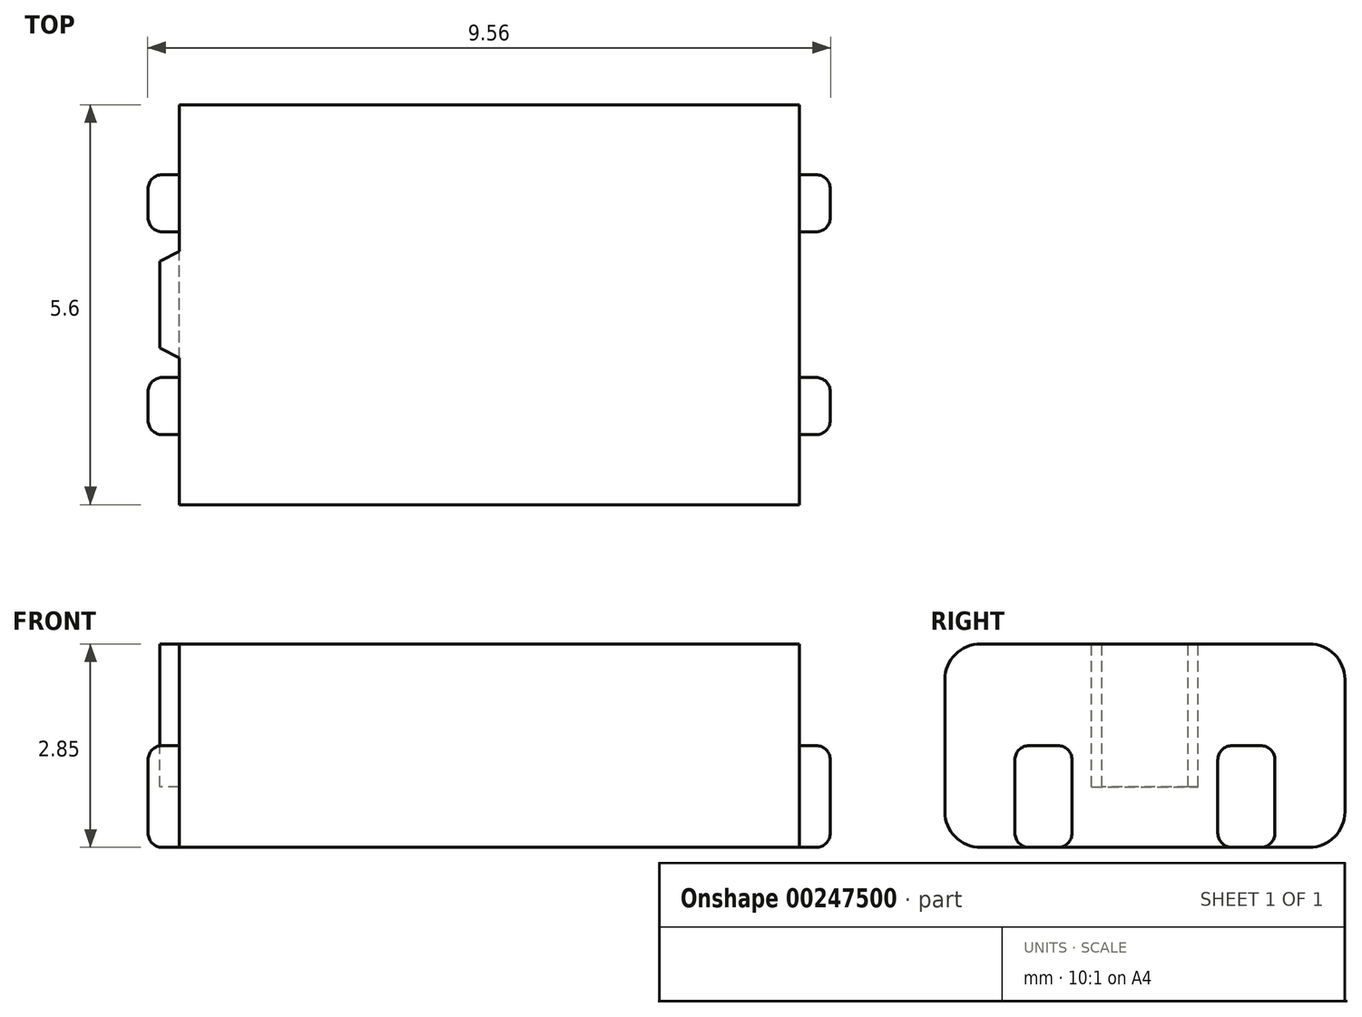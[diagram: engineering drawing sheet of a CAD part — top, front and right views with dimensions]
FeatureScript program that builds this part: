
annotation { "Feature Type Name" : "Feature", "Feature Type Description" : "" }
export const myFeature = defineFeature(function(context is Context, id is Id, definition is map)
    precondition{}
    {
        {
            var Q0;
            Q0=qCreatedBy(makeId("Top.planeOp"),FACE);
            var sketch = newSketch(context, id + "F0", { "sketchPlane" : qUnion([Q0])});
            skLineSegment(sketch, "E0.bottom", {"start": v(4.34, -2.8) * mm, "end": v(-4.34, -2.8) * mm});
            skLineSegment(sketch, "E0.top", {"start": v(4.34, 2.8) * mm, "end": v(-4.34, 2.8) * mm});
            skLineSegment(sketch, "E0.left", {"start": v(4.34, -2.8) * mm, "end": v(4.34, 2.8) * mm});
            skLineSegment(sketch, "E0.right", {"start": v(-4.34, -2.8) * mm, "end": v(-4.34, 2.8) * mm});
            skPoint(sketch, "E0.middle", {"position": v(0, 0) * mm});
            skSolve(sketch);
        }
        {
            var Q0;
            Q0=qSketchRegion(id+"F0",true);
            extrude(context, id + "F1", {"entities" : qUnion([Q0]), "depth" : 2.85 * mm});
        }
        {
            var Q0;
            Q0=makeQuery(id+"F1.opExtrude","CAP_FACE",FACE,{"disambiguationData":[OSD([sQuery(id+"F0.wireOp",EDGE,"E0.bottom"),sQuery(id+"F0.wireOp",EDGE,"E0.top"),sQuery(id+"F0.wireOp",EDGE,"E0.left"),sQuery(id+"F0.wireOp",EDGE,"E0.right")])],"isStart":true});
            var sketch = newSketch(context, id + "F2", { "sketchPlane" : qUnion([Q0])});
            skLineSegment(sketch, "E1", {"start": v(-5.81, 0) * mm, "end": v(7.13, 0) * mm, "construction": true});
            skPoint(sketch, "E1.endSnap0", {"position": v(-4.34, 0) * mm});
            skLineSegment(sketch, "E2", {"start": v(0, 3.67) * mm, "end": v(0, -3.67) * mm, "construction": true});
            skLineSegment(sketch, "E3.bottom", {"start": v(4.78, 1.02) * mm, "end": v(-4.78, 1.02) * mm});
            skLineSegment(sketch, "E3.top", {"start": v(4.78, 1.82) * mm, "end": v(-4.78, 1.82) * mm});
            skLineSegment(sketch, "E3.left", {"start": v(4.78, 1.02) * mm, "end": v(4.78, 1.82) * mm});
            skLineSegment(sketch, "E3.right", {"start": v(-4.78, 1.02) * mm, "end": v(-4.78, 1.82) * mm});
            skPoint(sketch, "E3.middle", {"position": v(0, 1.42) * mm});
            skLineSegment(sketch, "E4.MirrorCS", {"start": v(-4.77, -1.02) * mm, "end": v(-4.77, -1.82) * mm});
            skLineSegment(sketch, "E5.MirrorCS", {"start": v(4.78, -1.02) * mm, "end": v(-4.78, -1.02) * mm});
            skLineSegment(sketch, "E6.MirrorCS", {"start": v(4.78, -1.82) * mm, "end": v(-4.77, -1.82) * mm});
            skLineSegment(sketch, "E7.MirrorCS", {"start": v(4.78, -1.02) * mm, "end": v(4.78, -1.82) * mm});
            skPoint(sketch, "E8.MirrorP", {"position": v(0, -1.42) * mm});
            skSolve(sketch);
        }
        {
            var Q0;
            Q0=qSketchRegion(id+"F2",true);
            extrude(context, id + "F3", {"entities" : qUnion([Q0]), "operationType" : NewBodyOperationType.ADD, "oppositeDirection" : true, "depth" : (2.85 / 2) * mm});
        }
        {
            var Q0;
            Q0=makeQuery(id+"F1.opExtrude","CAP_FACE",FACE,{"disambiguationData":[OSD([sQuery(id+"F0.wireOp",EDGE,"E0.bottom"),sQuery(id+"F0.wireOp",EDGE,"E0.top"),sQuery(id+"F0.wireOp",EDGE,"E0.left"),sQuery(id+"F0.wireOp",EDGE,"E0.right")])],"isStart":false});
            var sketch = newSketch(context, id + "F4", { "sketchPlane" : qUnion([Q0])});
            skLineSegment(sketch, "E9", {"start": v(0, 0) * mm, "end": v(-6.58, 0) * mm, "construction": true});
            skLineSegment(sketch, "E10", {"start": v(-4.34, 0) * mm, "end": v(-4.34, 0.75) * mm});
            skLineSegment(sketch, "E11", {"start": v(-4.34, 0.75) * mm, "end": v(-4.61, 0.6) * mm});
            skLineSegment(sketch, "E12", {"start": v(-4.61, 0.6) * mm, "end": v(-4.61, 0) * mm});
            skLineSegment(sketch, "E13.MirrorCS", {"start": v(-4.34, 0) * mm, "end": v(-4.34, -0.75) * mm});
            skLineSegment(sketch, "E14.MirrorCS", {"start": v(-4.61, -0.6) * mm, "end": v(-4.61, 0) * mm});
            skLineSegment(sketch, "E15.MirrorCS", {"start": v(-4.34, -0.75) * mm, "end": v(-4.61, -0.6) * mm});
            skSolve(sketch);
        }
        {
            var Q0;
            Q0=qSketchRegion(id+"F4",true);
            extrude(context, id + "F5", {"entities" : qUnion([Q0]), "operationType" : NewBodyOperationType.ADD, "oppositeDirection" : true, "depth" : 2 * mm});
        }
        {
            var Q0;
            Q0=makeQuery(id+"F3.opExtrude","SWEPT_EDGE",EDGE,{"disambiguationData":[OSD([sQuery(id+"F2.wireOp",EDGE,"E4.MirrorCS"),sQuery(id+"F2.wireOp",EDGE,"E6.MirrorCS")])]});
            var Q1;
            Q1=makeQuery(id+"F3.opExtrude","SWEPT_EDGE",EDGE,{"disambiguationData":[OSD([sQuery(id+"F2.wireOp",EDGE,"E4.MirrorCS"),sQuery(id+"F2.wireOp",EDGE,"E5.MirrorCS")])]});
            var Q2;
            Q2=makeQuery(id+"F3.opExtrude","CAP_EDGE",EDGE,{"disambiguationData":[OSD([sQuery(id+"F2.wireOp",EDGE,"E4.MirrorCS")])],"isStart":false});
            var Q3;
            {var subQ1=sQuery(id+"F2.wireOp",EDGE,"E6.MirrorCS");Q3=makeQuery(id+"F3.boolean.opBoolean","SPLIT",EDGE,{"disambiguationData":[TD([makeQuery(id+"F1.opExtrude","SWEPT_FACE",FACE,{"disambiguationData":[OSD([sQuery(id+"F0.wireOp",EDGE,"E0.right")])]})])],"derivedFrom":makeQuery(id+"F3.opExtrude","CAP_EDGE",EDGE,{"disambiguationData":[OSD([subQ1])],"isStart":false})});}
            var Q4;
            {var subQ1=sQuery(id+"F2.wireOp",EDGE,"E5.MirrorCS");Q4=makeQuery(id+"F3.boolean.opBoolean","SPLIT",EDGE,{"disambiguationData":[TD([makeQuery(id+"F1.opExtrude","SWEPT_FACE",FACE,{"disambiguationData":[OSD([sQuery(id+"F0.wireOp",EDGE,"E0.right")])]})])],"derivedFrom":makeQuery(id+"F3.opExtrude","CAP_EDGE",EDGE,{"disambiguationData":[OSD([subQ1])],"isStart":false})});}
            var Q5;
            Q5=makeQuery(id+"F3.opExtrude","SWEPT_EDGE",EDGE,{"disambiguationData":[OSD([sQuery(id+"F2.wireOp",EDGE,"E3.bottom"),sQuery(id+"F2.wireOp",EDGE,"E3.right")])]});
            var Q6;
            Q6=makeQuery(id+"F3.opExtrude","CAP_EDGE",EDGE,{"disambiguationData":[OSD([sQuery(id+"F2.wireOp",EDGE,"E3.right")])],"isStart":false});
            var Q7;
            Q7=makeQuery(id+"F3.opExtrude","SWEPT_EDGE",EDGE,{"disambiguationData":[OSD([sQuery(id+"F2.wireOp",EDGE,"E3.top"),sQuery(id+"F2.wireOp",EDGE,"E3.right")])]});
            var Q8;
            {var subQ1=sQuery(id+"F2.wireOp",EDGE,"E3.top");Q8=makeQuery(id+"F3.boolean.opBoolean","SPLIT",EDGE,{"disambiguationData":[TD([makeQuery(id+"F1.opExtrude","SWEPT_FACE",FACE,{"disambiguationData":[OSD([sQuery(id+"F0.wireOp",EDGE,"E0.right")])]})])],"derivedFrom":makeQuery(id+"F3.opExtrude","CAP_EDGE",EDGE,{"disambiguationData":[OSD([subQ1])],"isStart":false})});}
            var Q9;
            {var subQ1=sQuery(id+"F2.wireOp",EDGE,"E3.bottom");Q9=makeQuery(id+"F3.boolean.opBoolean","SPLIT",EDGE,{"disambiguationData":[TD([makeQuery(id+"F1.opExtrude","SWEPT_FACE",FACE,{"disambiguationData":[OSD([sQuery(id+"F0.wireOp",EDGE,"E0.right")])]})])],"derivedFrom":makeQuery(id+"F3.opExtrude","CAP_EDGE",EDGE,{"disambiguationData":[OSD([subQ1])],"isStart":false})});}
            var Q10;
            Q10=makeQuery(id+"F3.opExtrude","CAP_EDGE",EDGE,{"disambiguationData":[OSD([sQuery(id+"F2.wireOp",EDGE,"E4.MirrorCS")])],"isStart":true});
            var Q11;
            {var subQ1=sQuery(id+"F0.wireOp",EDGE,"E0.right");var subQ2=sQuery(id+"F2.wireOp",EDGE,"E5.MirrorCS");Q11=makeQuery(id+"F3.boolean.opBoolean","SPLIT",EDGE,{"disambiguationData":[TD([makeQuery(id+"F1.opExtrude","SWEPT_FACE",FACE,{"disambiguationData":[OSD([subQ1])]})])],"derivedFrom":makeQuery(id+"F3.opExtrude","CAP_EDGE",EDGE,{"disambiguationData":[OSD([subQ2])],"isStart":true})});}
            var Q12;
            {var subQ1=sQuery(id+"F0.wireOp",EDGE,"E0.right");var subQ2=sQuery(id+"F2.wireOp",EDGE,"E6.MirrorCS");Q12=makeQuery(id+"F3.boolean.opBoolean","SPLIT",EDGE,{"disambiguationData":[TD([makeQuery(id+"F1.opExtrude","SWEPT_FACE",FACE,{"disambiguationData":[OSD([subQ1])]})])],"derivedFrom":makeQuery(id+"F3.opExtrude","CAP_EDGE",EDGE,{"disambiguationData":[OSD([subQ2])],"isStart":true})});}
            var Q13;
            {var subQ0=sQuery(id+"F0.wireOp",EDGE,"E0.right");var subQ1=sQuery(id+"F2.wireOp",EDGE,"E3.bottom");Q13=makeQuery(id+"F3.boolean.opBoolean","SPLIT",EDGE,{"disambiguationData":[TD([makeQuery(id+"F1.opExtrude","SWEPT_FACE",FACE,{"disambiguationData":[OSD([subQ0])]})])],"derivedFrom":makeQuery(id+"F3.opExtrude","CAP_EDGE",EDGE,{"disambiguationData":[OSD([subQ1])],"isStart":true})});}
            var Q14;
            Q14=makeQuery(id+"F3.opExtrude","CAP_EDGE",EDGE,{"disambiguationData":[OSD([sQuery(id+"F2.wireOp",EDGE,"E3.right")])],"isStart":true});
            var Q15;
            {var subQ0=sQuery(id+"F0.wireOp",EDGE,"E0.right");var subQ1=sQuery(id+"F2.wireOp",EDGE,"E3.top");Q15=makeQuery(id+"F3.boolean.opBoolean","SPLIT",EDGE,{"disambiguationData":[TD([makeQuery(id+"F1.opExtrude","SWEPT_FACE",FACE,{"disambiguationData":[OSD([subQ0])]})])],"derivedFrom":makeQuery(id+"F3.opExtrude","CAP_EDGE",EDGE,{"disambiguationData":[OSD([subQ1])],"isStart":true})});}
            var Q16;
            Q16=makeQuery(id+"F3.opExtrude","SWEPT_EDGE",EDGE,{"disambiguationData":[OSD([sQuery(id+"F2.wireOp",EDGE,"E3.top"),sQuery(id+"F2.wireOp",EDGE,"E3.left")])]});
            var Q17;
            Q17=makeQuery(id+"F3.opExtrude","CAP_EDGE",EDGE,{"disambiguationData":[OSD([sQuery(id+"F2.wireOp",EDGE,"E3.left")])],"isStart":false});
            var Q18;
            Q18=makeQuery(id+"F3.opExtrude","SWEPT_EDGE",EDGE,{"disambiguationData":[OSD([sQuery(id+"F2.wireOp",EDGE,"E3.bottom"),sQuery(id+"F2.wireOp",EDGE,"E3.left")])]});
            var Q19;
            {var subQ1=sQuery(id+"F2.wireOp",EDGE,"E3.top");Q19=makeQuery(id+"F3.boolean.opBoolean","SPLIT",EDGE,{"disambiguationData":[TD([makeQuery(id+"F1.opExtrude","SWEPT_FACE",FACE,{"disambiguationData":[OSD([sQuery(id+"F0.wireOp",EDGE,"E0.left")])]})])],"derivedFrom":makeQuery(id+"F3.opExtrude","CAP_EDGE",EDGE,{"disambiguationData":[OSD([subQ1])],"isStart":false})});}
            var Q20;
            {var subQ1=sQuery(id+"F2.wireOp",EDGE,"E3.bottom");Q20=makeQuery(id+"F3.boolean.opBoolean","SPLIT",EDGE,{"disambiguationData":[TD([makeQuery(id+"F1.opExtrude","SWEPT_FACE",FACE,{"disambiguationData":[OSD([sQuery(id+"F0.wireOp",EDGE,"E0.left")])]})])],"derivedFrom":makeQuery(id+"F3.opExtrude","CAP_EDGE",EDGE,{"disambiguationData":[OSD([subQ1])],"isStart":false})});}
            var Q21;
            Q21=makeQuery(id+"F3.opExtrude","SWEPT_EDGE",EDGE,{"disambiguationData":[OSD([sQuery(id+"F2.wireOp",EDGE,"E5.MirrorCS"),sQuery(id+"F2.wireOp",EDGE,"E7.MirrorCS")])]});
            var Q22;
            {var subQ1=sQuery(id+"F2.wireOp",EDGE,"E5.MirrorCS");Q22=makeQuery(id+"F3.boolean.opBoolean","SPLIT",EDGE,{"disambiguationData":[TD([makeQuery(id+"F1.opExtrude","SWEPT_FACE",FACE,{"disambiguationData":[OSD([sQuery(id+"F0.wireOp",EDGE,"E0.left")])]})])],"derivedFrom":makeQuery(id+"F3.opExtrude","CAP_EDGE",EDGE,{"disambiguationData":[OSD([subQ1])],"isStart":false})});}
            var Q23;
            Q23=makeQuery(id+"F3.opExtrude","CAP_EDGE",EDGE,{"disambiguationData":[OSD([sQuery(id+"F2.wireOp",EDGE,"E7.MirrorCS")])],"isStart":false});
            var Q24;
            {var subQ1=sQuery(id+"F2.wireOp",EDGE,"E6.MirrorCS");Q24=makeQuery(id+"F3.boolean.opBoolean","SPLIT",EDGE,{"disambiguationData":[TD([makeQuery(id+"F1.opExtrude","SWEPT_FACE",FACE,{"disambiguationData":[OSD([sQuery(id+"F0.wireOp",EDGE,"E0.left")])]})])],"derivedFrom":makeQuery(id+"F3.opExtrude","CAP_EDGE",EDGE,{"disambiguationData":[OSD([subQ1])],"isStart":false})});}
            var Q25;
            Q25=makeQuery(id+"F3.opExtrude","SWEPT_EDGE",EDGE,{"disambiguationData":[OSD([sQuery(id+"F2.wireOp",EDGE,"E6.MirrorCS"),sQuery(id+"F2.wireOp",EDGE,"E7.MirrorCS")])]});
            var Q26;
            {var subQ0=sQuery(id+"F0.wireOp",EDGE,"E0.left");var subQ2=sQuery(id+"F2.wireOp",EDGE,"E3.top");Q26=makeQuery(id+"F3.boolean.opBoolean","SPLIT",EDGE,{"disambiguationData":[TD([makeQuery(id+"F1.opExtrude","SWEPT_FACE",FACE,{"disambiguationData":[OSD([subQ0])]})])],"derivedFrom":makeQuery(id+"F3.opExtrude","CAP_EDGE",EDGE,{"disambiguationData":[OSD([subQ2])],"isStart":true})});}
            var Q27;
            Q27=makeQuery(id+"F3.opExtrude","CAP_EDGE",EDGE,{"disambiguationData":[OSD([sQuery(id+"F2.wireOp",EDGE,"E3.left")])],"isStart":true});
            var Q28;
            {var subQ0=sQuery(id+"F0.wireOp",EDGE,"E0.left");var subQ2=sQuery(id+"F2.wireOp",EDGE,"E3.bottom");Q28=makeQuery(id+"F3.boolean.opBoolean","SPLIT",EDGE,{"disambiguationData":[TD([makeQuery(id+"F1.opExtrude","SWEPT_FACE",FACE,{"disambiguationData":[OSD([subQ0])]})])],"derivedFrom":makeQuery(id+"F3.opExtrude","CAP_EDGE",EDGE,{"disambiguationData":[OSD([subQ2])],"isStart":true})});}
            var Q29;
            {var subQ1=sQuery(id+"F2.wireOp",EDGE,"E5.MirrorCS");var subQ2=sQuery(id+"F0.wireOp",EDGE,"E0.left");Q29=makeQuery(id+"F3.boolean.opBoolean","SPLIT",EDGE,{"disambiguationData":[TD([makeQuery(id+"F1.opExtrude","SWEPT_FACE",FACE,{"disambiguationData":[OSD([subQ2])]})])],"derivedFrom":makeQuery(id+"F3.opExtrude","CAP_EDGE",EDGE,{"disambiguationData":[OSD([subQ1])],"isStart":true})});}
            var Q30;
            Q30=makeQuery(id+"F3.opExtrude","CAP_EDGE",EDGE,{"disambiguationData":[OSD([sQuery(id+"F2.wireOp",EDGE,"E7.MirrorCS")])],"isStart":true});
            var Q31;
            {var subQ1=sQuery(id+"F2.wireOp",EDGE,"E6.MirrorCS");var subQ2=sQuery(id+"F0.wireOp",EDGE,"E0.left");Q31=makeQuery(id+"F3.boolean.opBoolean","SPLIT",EDGE,{"disambiguationData":[TD([makeQuery(id+"F1.opExtrude","SWEPT_FACE",FACE,{"disambiguationData":[OSD([subQ2])]})])],"derivedFrom":makeQuery(id+"F3.opExtrude","CAP_EDGE",EDGE,{"disambiguationData":[OSD([subQ1])],"isStart":true})});}
            fillet(context, id + "F6", {"entities" : qUnion([Q0, Q1, Q2, Q3, Q4, Q5, Q6, Q7, Q8, Q9, Q10, Q11, Q12, Q13, Q14, Q15, Q16, Q17, Q18, Q19, Q20, Q21, Q22, Q23, Q24, Q25, Q26, Q27, Q28, Q29, Q30, Q31]), "radius" : .2 * mm, "tangentPropagation" : true, "allowEdgeOverflow" : false});
        }
        {
            var Q0;
            Q0=makeQuery(id+"F1.opExtrude","CAP_EDGE",EDGE,{"disambiguationData":[OSD([sQuery(id+"F0.wireOp",EDGE,"E0.bottom")])],"isStart":false});
            var Q1;
            Q1=makeQuery(id+"F1.opExtrude","CAP_EDGE",EDGE,{"disambiguationData":[OSD([sQuery(id+"F0.wireOp",EDGE,"E0.top")])],"isStart":false});
            var Q2;
            Q2=makeQuery(id+"F1.opExtrude","CAP_EDGE",EDGE,{"disambiguationData":[OSD([sQuery(id+"F0.wireOp",EDGE,"E0.top")])],"isStart":true});
            var Q3;
            Q3=makeQuery(id+"F1.opExtrude","CAP_EDGE",EDGE,{"disambiguationData":[OSD([sQuery(id+"F0.wireOp",EDGE,"E0.bottom")])],"isStart":true});
            fillet(context, id + "F7", {"entities" : qUnion([Q0, Q1, Q2, Q3]), "radius" : .5 * mm, "tangentPropagation" : true, "allowEdgeOverflow" : false});
        }
    });
